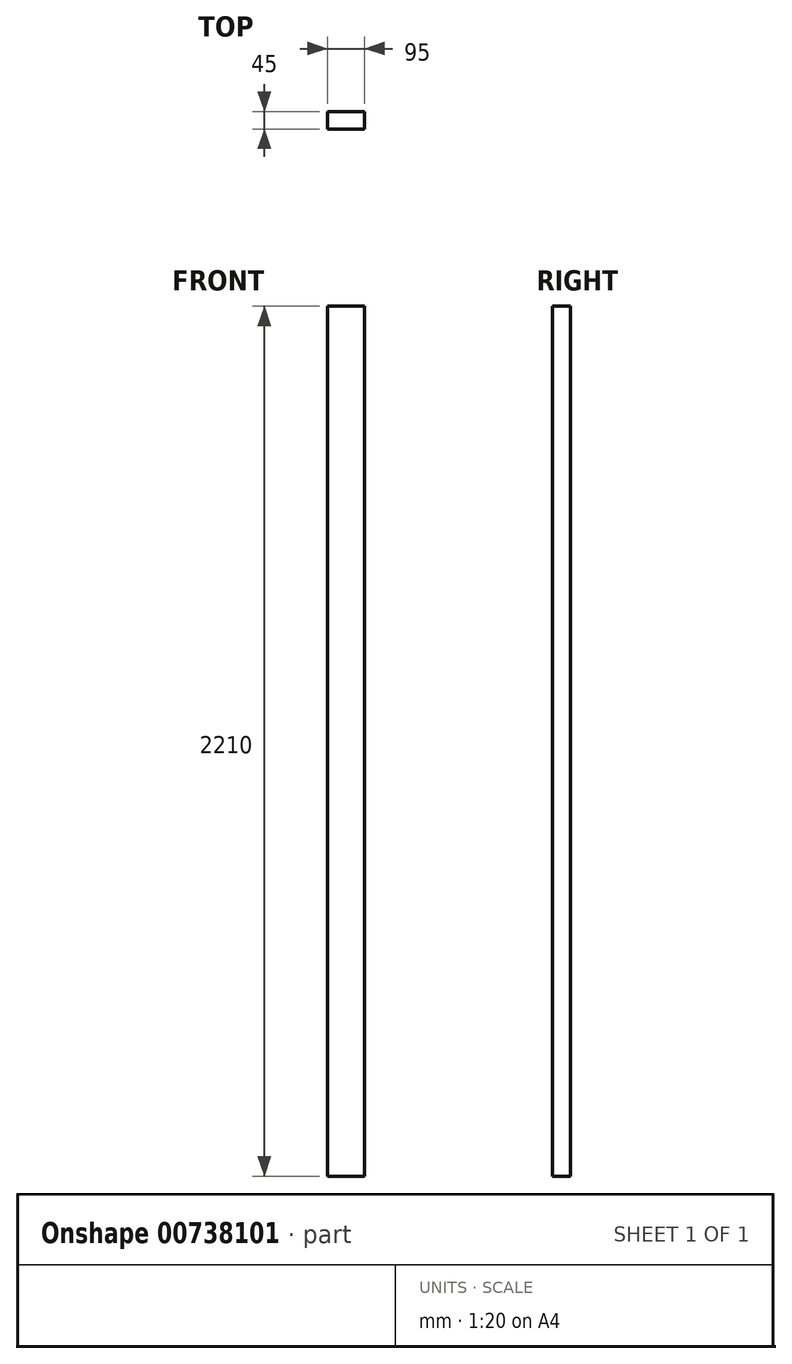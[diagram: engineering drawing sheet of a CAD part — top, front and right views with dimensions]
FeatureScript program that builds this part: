
annotation { "Feature Type Name" : "Feature", "Feature Type Description" : "" }
export const myFeature = defineFeature(function(context is Context, id is Id, definition is map)
    precondition{}
    {
        {
            var Q0;
            Q0=qCreatedBy(makeId("Front.planeOp"),FACE);
            var sketch = newSketch(context, id + "F0", { "sketchPlane" : qUnion([Q0])});
            skLineSegment(sketch, "E0.bottom", {"start": v(-30.03, 2173.26) * mm, "end": v(64.97, 2173.26) * mm});
            skLineSegment(sketch, "E0.top", {"start": v(-30.03, -36.74) * mm, "end": v(64.97, -36.74) * mm});
            skLineSegment(sketch, "E0.left", {"start": v(-30.03, 2173.26) * mm, "end": v(-30.03, -36.74) * mm});
            skLineSegment(sketch, "E0.right", {"start": v(64.97, 2173.26) * mm, "end": v(64.97, -36.74) * mm});
            skSolve(sketch);
        }
        {
            var Q0;
            Q0=makeQuery(id+"F0.imprint","IMPRINT",FACE,{"disambiguationData":[TD([[makeQuery(id+"F0.imprint","IMPRINT",EDGE,{"derivedFrom":sQuery(id+"F0.wireOp",EDGE,"E0.bottom")}),-1.0]])]});
            extrude(context, id + "F1", {"entities" : qUnion([Q0]), "depth" : 45 * mm, "offsetDistance" : 25 * mm});
        }
    });
